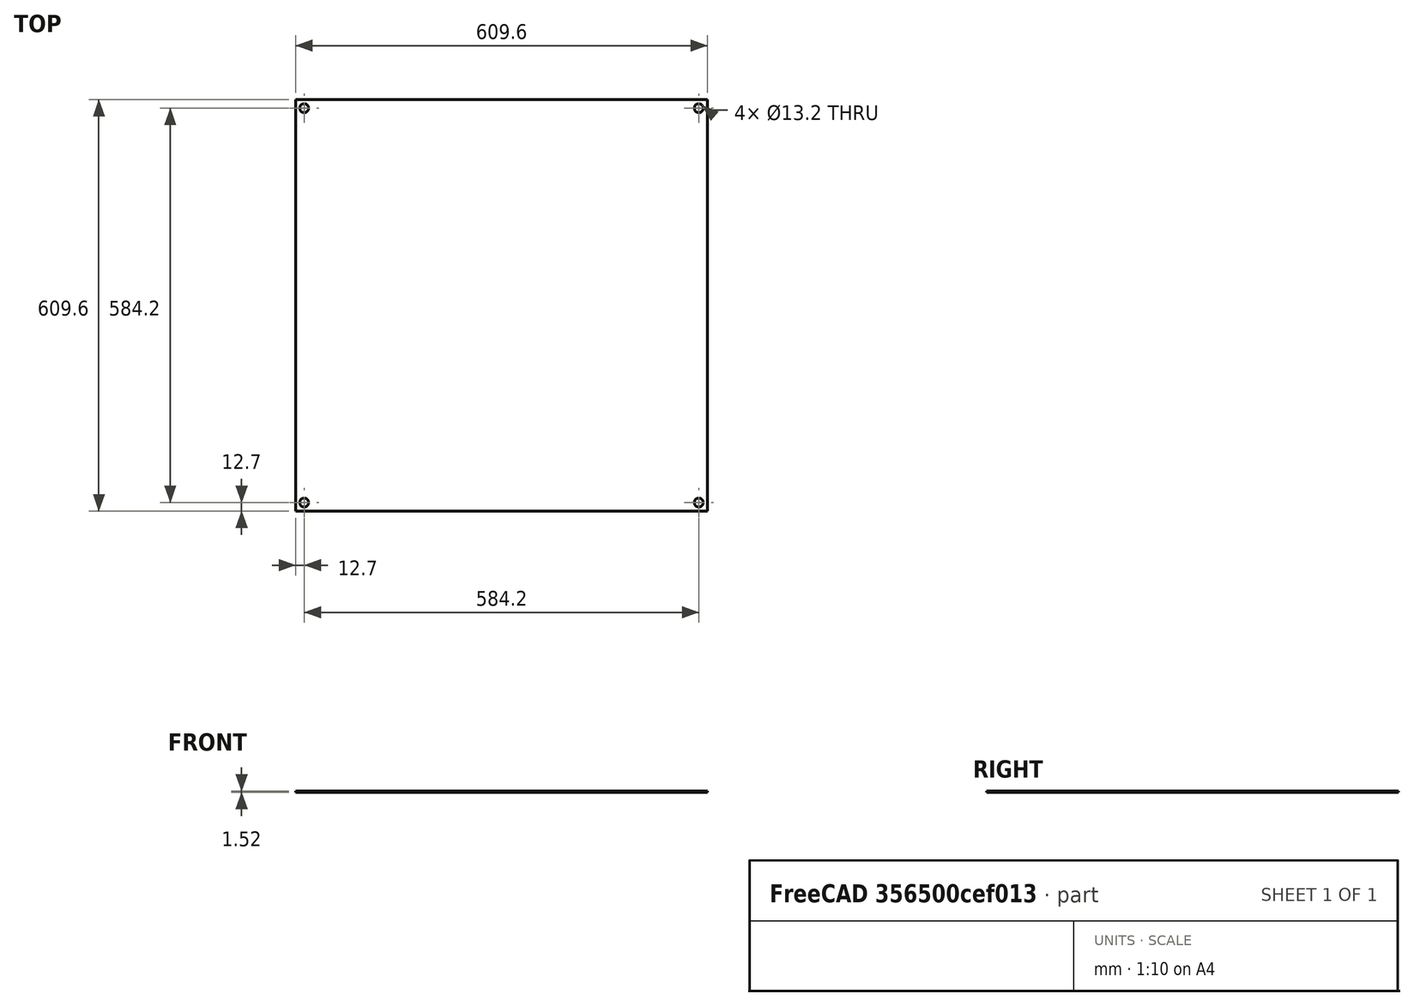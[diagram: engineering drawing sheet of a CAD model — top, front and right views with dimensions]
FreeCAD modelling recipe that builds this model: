
FCSTD DOCUMENT  (FreeCAD 0.21R33694 (Git))
Label: Steel_Sheet_24inx24inx16ga
License: All rights reserved
LicenseURL: http://en.wikipedia.org/wiki/All_rights_reserved
objects: Sketcher::SketchObject×1, PartDesign::Pad×1, PartDesign::Body×1
note: 4 computed .brp shape members not serialized (recipe doc carries the construction recipe); baked Part::Feature solids carry a one-line shape summary decoded from their .brp

FEATURE [Sketcher::SketchObject] Sketch
  FullyConstrained = true
  MapMode = 5
  Support = -> [XY_Plane]
  sketch-geometry (16):
    g0: LineSegment StartX=-304.8 StartY=304.8 StartZ=0 EndX=304.8 EndY=304.8 EndZ=0
    g1: LineSegment StartX=304.8 StartY=304.8 StartZ=0 EndX=304.8 EndY=-304.8 EndZ=0
    g2: LineSegment StartX=304.8 StartY=-304.8 StartZ=0 EndX=-304.8 EndY=-304.8 EndZ=0
    g3: LineSegment StartX=-304.8 StartY=-304.8 StartZ=0 EndX=-304.8 EndY=304.8 EndZ=0
    g4: LineSegment StartX=304.8 StartY=304.8 StartZ=0 EndX=292.1 EndY=304.8 EndZ=0
    g5: LineSegment StartX=292.1 StartY=304.8 StartZ=0 EndX=292.1 EndY=292.1 EndZ=0
    g6: Circle CenterX=292.1 CenterY=292.1 CenterZ=0 NormalX=0 NormalY=0 NormalZ=1 AngleXU=0 Radius=6.6
    g7: LineSegment StartX=-304.8 StartY=304.8 StartZ=0 EndX=-292.1 EndY=304.8 EndZ=0
    g8: LineSegment StartX=-292.1 StartY=304.8 StartZ=0 EndX=-292.1 EndY=292.1 EndZ=0
    g9: Circle CenterX=-292.1 CenterY=292.1 CenterZ=0 NormalX=0 NormalY=0 NormalZ=1 AngleXU=0 Radius=6.6
    g10: LineSegment StartX=-304.8 StartY=-304.8 StartZ=0 EndX=-292.1 EndY=-304.8 EndZ=0
    g11: LineSegment StartX=-292.1 StartY=-304.8 StartZ=0 EndX=-292.1 EndY=-292.1 EndZ=0
    g12: Circle CenterX=-292.1 CenterY=-292.1 CenterZ=0 NormalX=0 NormalY=0 NormalZ=1 AngleXU=0 Radius=6.6
    g13: LineSegment StartX=304.8 StartY=-304.8 StartZ=0 EndX=292.1 EndY=-304.8 EndZ=0
    g14: LineSegment StartX=292.1 StartY=-304.8 StartZ=0 EndX=292.1 EndY=-292.1 EndZ=0
    g15: Circle CenterX=292.1 CenterY=-292.1 CenterZ=0 NormalX=0 NormalY=0 NormalZ=1 AngleXU=0 Radius=6.6
  constraints (43):
    c: Coincident(g0,g1)
    c: Coincident(g1,g2)
    c: Coincident(g2,g3)
    c: Coincident(g3,g0)
    c: Horizontal(g0)
    c: Horizontal(g2)
    c: Vertical(g1)
    c: Vertical(g3)
    c: Symmetric(g2,g0,g-1)
    c: Equal(g1,g0)
    c: DistanceX(g0,g0) = 609.6
    c: Coincident(g4,g5)
    c: Horizontal(g4)
    c: Vertical(g5)
    c: Coincident(g4,g0)
    c: Equal(g4,g5)
    c: DistanceX(g4,g4) = 12.7
    c: Coincident(g6,g5)
    c: Radius(g6) = 6.6
    c: Coincident(g7,g8)
    c: Horizontal(g7)
    c: Vertical(g8)
    c: Coincident(g7,g0)
    c: Equal(g7,g8)
    c: Coincident(g9,g8)
    c: Equal(g4,g7)
    c: Equal(g9,g6)
    c: Coincident(g10,g11)
    c: Horizontal(g10)
    c: Vertical(g11)
    c: Coincident(g10,g2)
    c: Equal(g10,g11)
    c: Equal(g4,g10)
    c: Coincident(g12,g11)
    c: Equal(g6,g12)
    c: Coincident(g13,g14)
    c: Horizontal(g13)
    c: Vertical(g14)
    c: Coincident(g13,g1)
    c: Equal(g13,g14)
    c: Equal(g4,g13)
    c: Coincident(g15,g14)
    c: Equal(g6,g15)
FEATURE [PartDesign::Pad] Pad
  Direction = (0,0,1)
  Length = 1.519
  Length2 = 10
  Profile = -> Sketch
  ReferenceAxis = -> Sketch [N_Axis]
  Type = 0
FEATURE [PartDesign::Body] Body
  Group = -> [Sketch,Pad]
  Origin = -> Origin
  Tip = -> Pad
